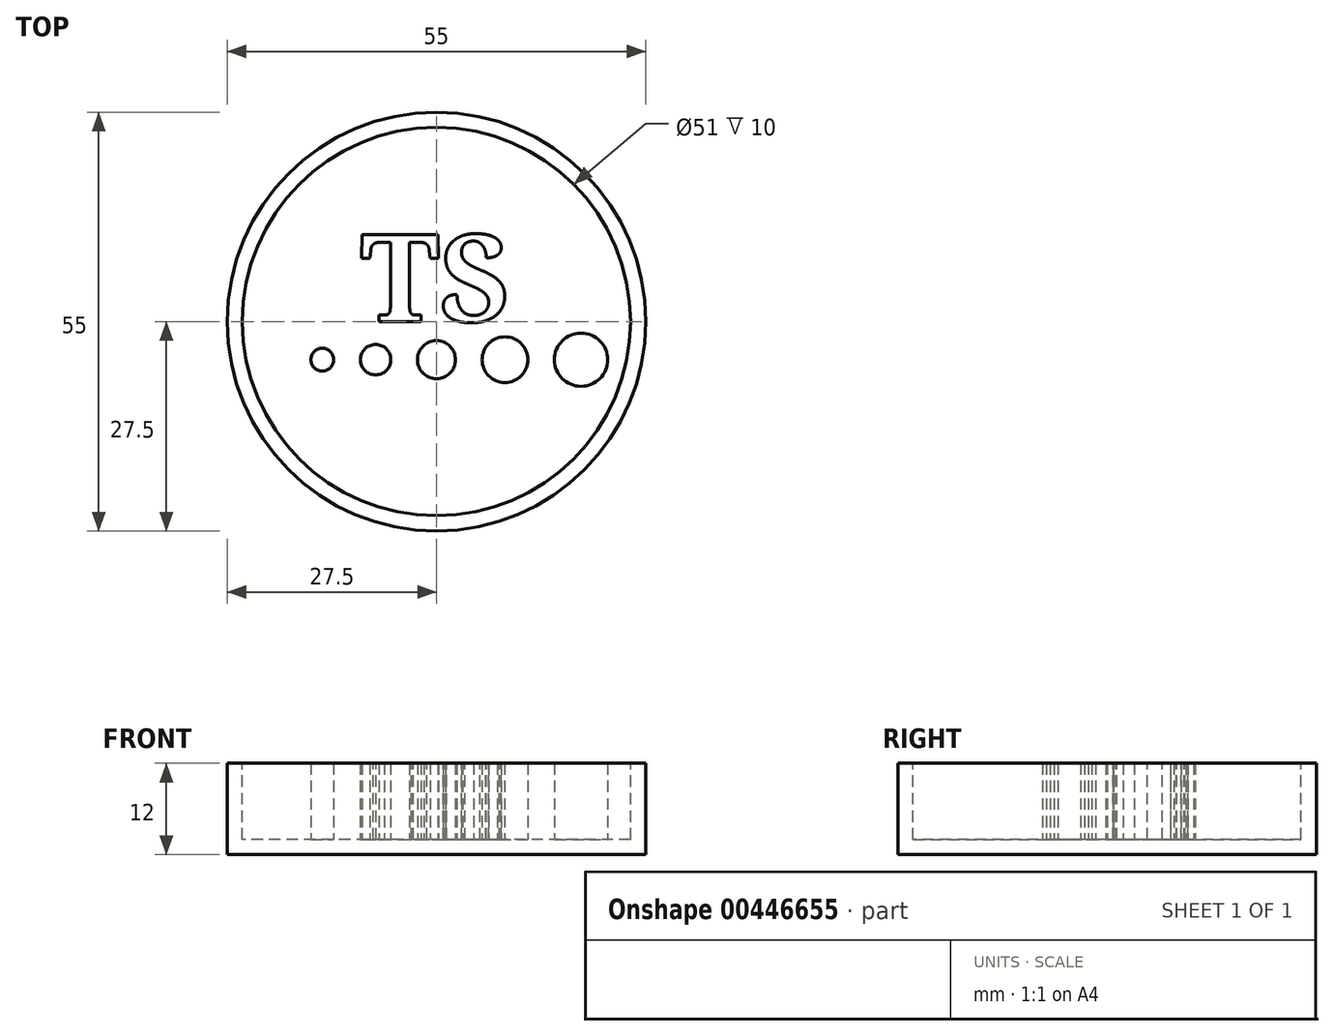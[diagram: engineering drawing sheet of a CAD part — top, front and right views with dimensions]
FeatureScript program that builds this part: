
annotation { "Feature Type Name" : "Feature", "Feature Type Description" : "" }
export const myFeature = defineFeature(function(context is Context, id is Id, definition is map)
    precondition{}
    {
        {
            var Q0;
            Q0=qCreatedBy(makeId("Front.planeOp"),FACE);
            var sketch = newSketch(context, id + "F0", { "sketchPlane" : qUnion([Q0])});
            skLineSegment(sketch, "E0", {"start": v(0, 0) * mm, "end": v(27.5, 0) * mm});
            skLineSegment(sketch, "E1", {"start": v(27.5, 0) * mm, "end": v(27.5, 12) * mm});
            skLineSegment(sketch, "E2", {"start": v(27.5, 12) * mm, "end": v(25.5, 12) * mm});
            skLineSegment(sketch, "E3", {"start": v(25.5, 12) * mm, "end": v(25.5, 2) * mm});
            skLineSegment(sketch, "E4", {"start": v(25.5, 2) * mm, "end": v(0, 2) * mm});
            skLineSegment(sketch, "E5", {"start": v(0, 2) * mm, "end": v(0, 0) * mm});
            skSolve(sketch);
        }
        {
            var Q0;
            Q0 = qSketchRegion(id + "F0", true);
            var Q1;
            Q1=sQuery(id+"F0.wireOp",EDGE,"E5");
            revolve(context, id + "F1", {"entities" : qUnion([Q0]), "axis" : qUnion([Q1]), "revolveType" : RevolveType.FULL});
        }
        {
            var Q0;
            Q0=makeQuery(id+"F1.opRevolve","SWEPT_FACE",FACE,{"disambiguationData":[OSD([sQuery(id+"F0.wireOp",EDGE,"E4")])]});
            var sketch = newSketch(context, id + "F2", { "sketchPlane" : qUnion([Q0])});
            skText(sketch, "E6", { "text": "TS \n", "fontName": "NotoSerif-Bold.ttf"});
            skCircle(sketch, "E7", {"center": v(0, -5) * mm, "radius": 2.5 * mm});
            skCircle(sketch, "E8", {"center": v(9, -5) * mm, "radius": 3 * mm});
            skCircle(sketch, "E9", {"center": v(19, -5) * mm, "radius": 3.5 * mm});
            skCircle(sketch, "E10", {"center": v(-15, -5) * mm, "radius": 1.5 * mm});
            skCircle(sketch, "E11", {"center": v(-8, -5) * mm, "radius": 2 * mm});
            const initialGuessF2  = {"E6": [-0.01, 0, 1, 0, 0.01149]};
            skSetInitialGuess(sketch, initialGuessF2);
            skSolve(sketch);
        }
        {
            var Q0;
            Q0 = qSketchRegion(id + "F2", true);
            extrude(context, id + "F3", {"entities" : qUnion([Q0]), "operationType" : NewBodyOperationType.ADD, "depth" : 10 * mm});
        }
    });
